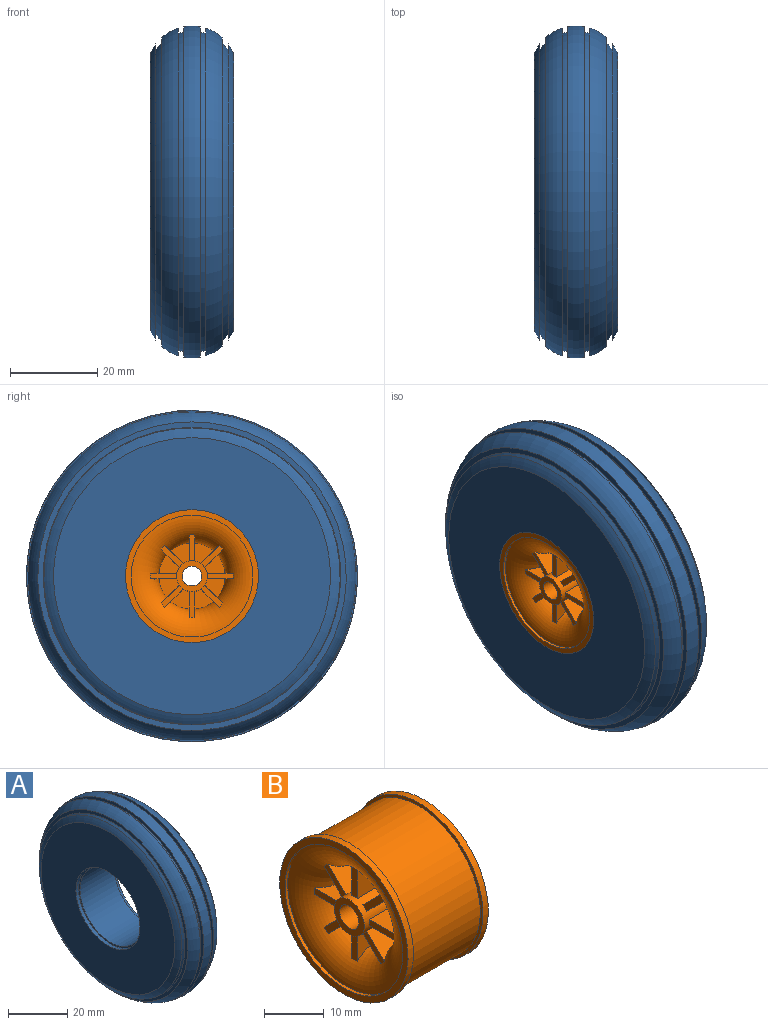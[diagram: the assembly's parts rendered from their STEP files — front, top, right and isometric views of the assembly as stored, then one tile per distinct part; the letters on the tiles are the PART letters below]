
ASSEMBLY  parts=2 mates=1
PART A: 24 faces, bbox 20.6x82.5x82.5 mm
  f0: cylinder r=15.24mm len=30.48mm, axis (-1,0,0), area 121.6mm2, adj f1,f23
  f1: plane 63.5x63.5mm, normal (1,0,0), area 2437.3mm2, adj f0,f2
  f2: torus R=27.78mm, axis (-1,0,0), area 530.3mm2, adj f1,f3
  f3: plane 67.95x67.95mm, normal (-1,0,0), area 266mm2, adj f2,f4
  f4: torus R=26.51mm, axis (-1,0,0), area 398.1mm2, adj f3,f5
  f5: plane 70.75x70.75mm, normal (1,0,0), area 277.2mm2, adj f4,f6
  f6: torus R=27.78mm, axis (-1,0,0), area 1023mm2, adj f5,f7
  f7: plane 75.2x75.2mm, normal (-1,0,0), area 295mm2, adj f6,f8
  f8: torus R=26.51mm, axis (-1,0,0), area 300.8mm2, adj f7,f9
  f9: plane 75.85x75.85mm, normal (1,0,0), area 297.5mm2, adj f8,f10
  f10: torus R=27.78mm, axis (-1,0,0), area 915.9mm2, adj f9,f11
  f11: plane 75.85x75.85mm, normal (-1,0,0), area 297.5mm2, adj f10,f12
  f12: torus R=26.51mm, axis (-1,0,0), area 300.8mm2, adj f11,f13
  f13: plane 75.2x75.2mm, normal (1,0,0), area 295mm2, adj f12,f14
  f14: torus R=27.78mm, axis (-1,0,0), area 1023mm2, adj f13,f15
  f15: plane 70.75x70.75mm, normal (-1,0,0), area 277.2mm2, adj f14,f16
  f16: torus R=26.51mm, axis (-1,0,0), area 398.1mm2, adj f15,f17
  f17: plane 67.95x67.95mm, normal (1,0,0), area 266mm2, adj f16,f18
  f18: torus R=27.78mm, axis (-1,0,0), area 530.3mm2, adj f17,f19
  f19: plane 63.5x63.5mm, normal (-1,0,0), area 2437.3mm2, adj f18,f20
  f20: cylinder r=15.24mm len=30.48mm, axis (-1,0,0), area 121.6mm2, adj f19,f21
  f21: plane 30.48x30.48mm, normal (-1,0,0), area 59.5mm2, adj f20,f22
  f22: cylinder r=14.61mm len=29.21mm, axis (-1,0,0), area 1515.1mm2, adj f21,f23
  f23: plane 30.48x30.48mm, normal (1,0,0), area 59.5mm2, adj f0,f22
PART B: 80 faces, bbox 19.1x40.1x40.1 mm
  f0: plane 4.67x4.29mm, normal (-1,0,0), area 12.7mm2, adj f14,f16,f72,f79
  f1: plane 4.67x4.29mm, normal (1,0,0), area 12.7mm2, adj f20,f22,f69,f76
  f2: plane 4.67x4.29mm, normal (-1,0,0), area 12.7mm2, adj f14,f16,f66,f73
  f3: plane 4.67x4.29mm, normal (1,0,0), area 12.7mm2, adj f20,f22,f63,f70
  f4: plane 4.67x4.29mm, normal (-1,0,0), area 12.7mm2, adj f14,f16,f60,f67
  f5: plane 4.67x4.29mm, normal (1,0,0), area 12.7mm2, adj f20,f22,f57,f64
  f6: plane 4.67x4.29mm, normal (-1,0,0), area 12.7mm2, adj f14,f16,f54,f61
  f7: plane 4.67x4.29mm, normal (1,0,0), area 12.7mm2, adj f20,f22,f51,f58
  f8: plane 4.67x4.29mm, normal (-1,0,0), area 12.7mm2, adj f14,f16,f48,f55
  f9: plane 4.67x4.29mm, normal (1,0,0), area 12.7mm2, adj f20,f22,f45,f52
  f10: plane 4.67x4.29mm, normal (-1,0,0), area 12.7mm2, adj f14,f16,f42,f49
  f11: plane 4.67x4.29mm, normal (1,0,0), area 12.7mm2, adj f20,f22,f39,f46
  f12: plane 4.67x4.29mm, normal (-1,0,0), area 12.7mm2, adj f14,f16,f36,f43
  f13: plane 4.67x4.29mm, normal (1,0,0), area 12.7mm2, adj f20,f22,f33,f40
  f14: torus R=13.97mm, axis (-1,0,0), area 572.8mm2, adj f0,f2,f4,f6,f8,f10,f12,f15
  f15: plane 4.67x4.29mm, normal (-1,0,0), area 12.7mm2, adj f14,f16,f37,f78
  f16: cylinder r=3.56mm len=7.11mm, axis (-1,0,0), area 81.8mm2, adj f0,f2,f4,f6,f8,f10,f12,f15
  f17: plane 7.11x7.11mm, normal (-1,0,0), area 23.7mm2, adj f16,f18
  f18: cylinder r=2.26mm len=16.51mm, axis (-1,0,0), area 234.5mm2, adj f17,f19
  f19: plane 7.11x7.11mm, normal (1,0,0), area 23.7mm2, adj f18,f20
  f20: cylinder r=3.56mm len=7.11mm, axis (-1,0,0), area 81.8mm2, adj f1,f3,f5,f7,f9,f11,f13,f19
  f21: plane 4.67x4.29mm, normal (1,0,0), area 12.7mm2, adj f20,f22,f34,f75
  f22: torus R=13.97mm, axis (-1,0,0), area 572.8mm2, adj f1,f3,f5,f7,f9,f11,f13,f21
  f23: cylinder r=13.97mm len=27.94mm, axis (-1,0,0), area 55.7mm2, adj f22,f24
  f24: plane 30.48x30.48mm, normal (1,0,0), area 116.5mm2, adj f23,f25
  f25: cylinder r=15.24mm len=30.48mm, axis (-1,0,0), area 121.6mm2, adj f24,f26
  f26: plane 30.48x30.48mm, normal (-1,0,0), area 59.5mm2, adj f25,f27
  f27: cylinder r=14.61mm len=29.21mm, axis (-1,0,0), area 1515.1mm2, adj f26,f28
  f28: plane 30.48x30.48mm, normal (1,0,0), area 59.5mm2, adj f27,f29
  f29: cylinder r=15.24mm len=30.48mm, axis (-1,0,0), area 121.6mm2, adj f28,f30
  f30: plane 30.48x30.48mm, normal (-1,0,0), area 116.5mm2, adj f29,f31
  f31: cylinder r=13.97mm len=27.94mm, axis (-1,0,0), area 55.7mm2, adj f14,f30
  f32: plane 5.98x1.27mm, normal (1,0,0), area 7.5mm2, adj f20,f22,f33,f34
  f33: plane 6.02x4.55mm, normal (0,0,1), area 21mm2, adj f13,f20,f22,f32
  f34: plane 6.02x4.55mm, normal (0,0,-1), area 21mm2, adj f20,f21,f22,f32
  f35: plane 5.98x1.27mm, normal (-1,0,0), area 7.5mm2, adj f14,f16,f36,f37
  f36: plane 6.02x4.55mm, normal (0,0,1), area 21mm2, adj f12,f14,f16,f35
  f37: plane 6.02x4.55mm, normal (0,0,-1), area 21mm2, adj f14,f15,f16,f35
  f38: plane 5.11x5.11mm, normal (1,0,0), area 7.5mm2, adj f20,f22,f39,f40
  f39: plane 4.54x4.27mm, normal (0,-0.71,0.71), area 21mm2, adj f11,f20,f22,f38
  f40: plane 4.54x4.27mm, normal (0,0.71,-0.71), area 21mm2, adj f13,f20,f22,f38
  f41: plane 5.11x5.11mm, normal (-1,0,0), area 7.5mm2, adj f14,f16,f42,f43
  f42: plane 4.54x4.27mm, normal (0,-0.71,0.71), area 21mm2, adj f10,f14,f16,f41
  f43: plane 4.54x4.27mm, normal (0,0.71,-0.71), area 21mm2, adj f12,f14,f16,f41
  f44: plane 5.98x1.27mm, normal (1,0,0), area 7.5mm2, adj f20,f22,f45,f46
  f45: plane 6.02x4.55mm, normal (0,-1,0), area 21mm2, adj f9,f20,f22,f44
  f46: plane 6.02x4.55mm, normal (0,1,0), area 21mm2, adj f11,f20,f22,f44
  f47: plane 5.98x1.27mm, normal (-1,0,0), area 7.5mm2, adj f14,f16,f48,f49
  f48: plane 6.02x4.55mm, normal (0,-1,0), area 21mm2, adj f8,f14,f16,f47
  f49: plane 6.02x4.55mm, normal (0,1,0), area 21mm2, adj f10,f14,f16,f47
  f50: plane 5.11x5.11mm, normal (1,0,0), area 7.5mm2, adj f20,f22,f51,f52
  f51: plane 4.54x4.27mm, normal (0,-0.71,-0.71), area 21mm2, adj f7,f20,f22,f50
  f52: plane 4.54x4.27mm, normal (0,0.71,0.71), area 21mm2, adj f9,f20,f22,f50
  f53: plane 5.11x5.11mm, normal (-1,0,0), area 7.5mm2, adj f14,f16,f54,f55
  f54: plane 4.54x4.27mm, normal (0,-0.71,-0.71), area 21mm2, adj f6,f14,f16,f53
  f55: plane 4.54x4.27mm, normal (0,0.71,0.71), area 21mm2, adj f8,f14,f16,f53
  f56: plane 5.98x1.27mm, normal (1,0,0), area 7.5mm2, adj f20,f22,f57,f58
  f57: plane 6.02x4.55mm, normal (0,0,-1), area 21mm2, adj f5,f20,f22,f56
  f58: plane 6.02x4.55mm, normal (0,0,1), area 21mm2, adj f7,f20,f22,f56
  f59: plane 5.98x1.27mm, normal (-1,0,0), area 7.5mm2, adj f14,f16,f60,f61
  f60: plane 6.02x4.55mm, normal (0,0,-1), area 21mm2, adj f4,f14,f16,f59
  f61: plane 6.02x4.55mm, normal (0,0,1), area 21mm2, adj f6,f14,f16,f59
  f62: plane 5.11x5.11mm, normal (1,0,0), area 7.5mm2, adj f20,f22,f63,f64
  f63: plane 4.54x4.27mm, normal (0,0.71,-0.71), area 21mm2, adj f3,f20,f22,f62
  f64: plane 4.54x4.27mm, normal (0,-0.71,0.71), area 21mm2, adj f5,f20,f22,f62
  f65: plane 5.11x5.11mm, normal (-1,0,0), area 7.5mm2, adj f14,f16,f66,f67
  f66: plane 4.54x4.27mm, normal (0,0.71,-0.71), area 21mm2, adj f2,f14,f16,f65
  f67: plane 4.54x4.27mm, normal (0,-0.71,0.71), area 21mm2, adj f4,f14,f16,f65
  f68: plane 5.98x1.27mm, normal (1,0,0), area 7.5mm2, adj f20,f22,f69,f70
  f69: plane 6.02x4.55mm, normal (0,1,0), area 21mm2, adj f1,f20,f22,f68
  f70: plane 6.02x4.55mm, normal (0,-1,0), area 21mm2, adj f3,f20,f22,f68
  f71: plane 5.98x1.27mm, normal (-1,0,0), area 7.5mm2, adj f14,f16,f72,f73
  f72: plane 6.02x4.55mm, normal (0,1,0), area 21mm2, adj f0,f14,f16,f71
  f73: plane 6.02x4.55mm, normal (0,-1,0), area 21mm2, adj f2,f14,f16,f71
  f74: plane 5.11x5.11mm, normal (1,0,0), area 7.5mm2, adj f20,f22,f75,f76
  f75: plane 4.54x4.27mm, normal (0,0.71,0.71), area 21mm2, adj f20,f21,f22,f74
  f76: plane 4.54x4.27mm, normal (0,-0.71,-0.71), area 21mm2, adj f1,f20,f22,f74
  f77: plane 5.11x5.11mm, normal (-1,0,0), area 7.5mm2, adj f14,f16,f78,f79
  f78: plane 4.54x4.27mm, normal (0,0.71,0.71), area 21mm2, adj f14,f15,f16,f77
  f79: plane 4.54x4.27mm, normal (0,-0.71,-0.71), area 21mm2, adj f0,f14,f16,f77
PLACE A t=(-11.35,-5.02,2.3)mm
PLACE B t=(-11.35,-5.02,2.3)mm
MATE fastened A.f0 <-> B.f14  axis (-1,0,0) through (-11.35,-5.02,2.3)mm
